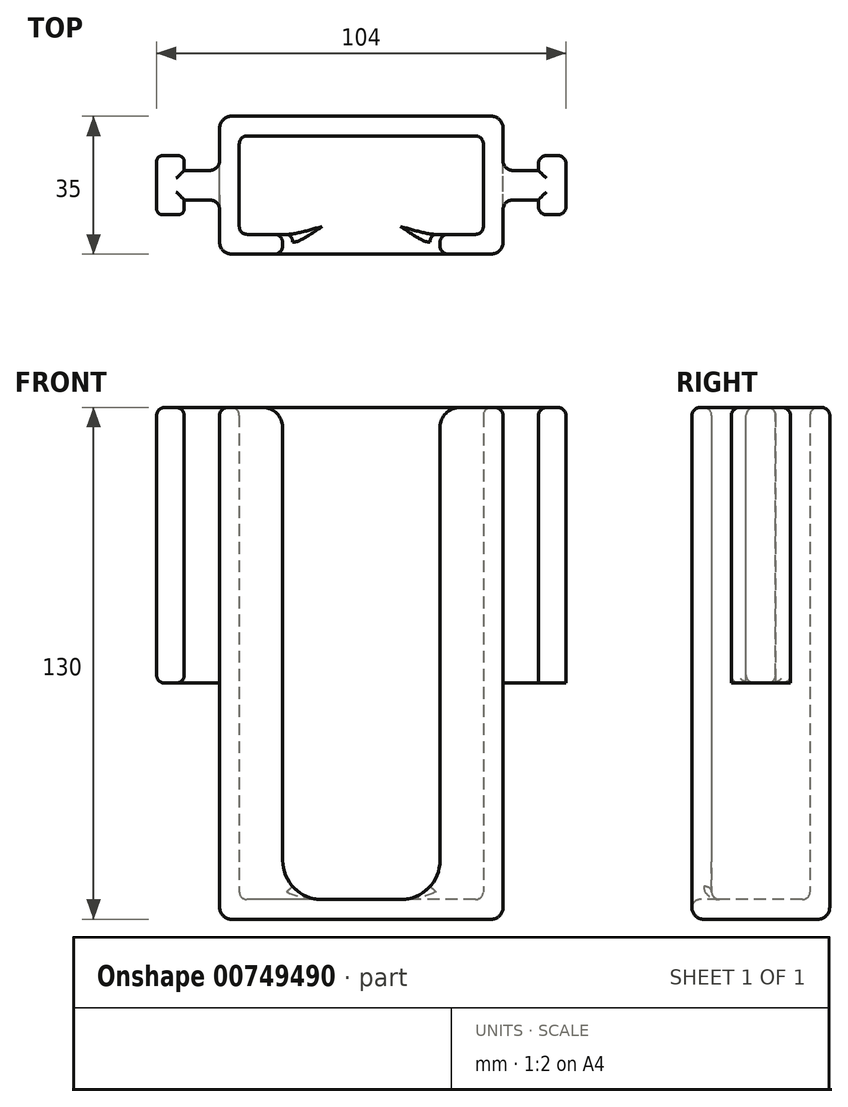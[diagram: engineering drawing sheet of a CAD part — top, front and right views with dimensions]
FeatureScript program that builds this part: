
annotation { "Feature Type Name" : "Feature", "Feature Type Description" : "" }
export const myFeature = defineFeature(function(context is Context, id is Id, definition is map)
    precondition{}
    {
        {
            var Q0;
            Q0=qCreatedBy(makeId("Top.planeOp"),FACE);
            var sketch = newSketch(context, id + "F0", { "sketchPlane" : qUnion([Q0])});
            skLineSegment(sketch, "E0.bottom", {"start": v(-36, -17.5) * mm, "end": v(-20, -17.5) * mm});
            skLineSegment(sketch, "E0.top", {"start": v(-36, 17.5) * mm, "end": v(36, 17.5) * mm});
            skLineSegment(sketch, "E0.left", {"start": v(-36, -17.5) * mm, "end": v(-36, 17.5) * mm});
            skLineSegment(sketch, "E0.right", {"start": v(36, -17.5) * mm, "end": v(36, 17.5) * mm});
            skPoint(sketch, "E0.middle", {"position": v(0, 0) * mm});
            skLineSegment(sketch, "E1.0", {"start": v(-31, 12.5) * mm, "end": v(31, 12.5) * mm});
            skLineSegment(sketch, "E2.0", {"start": v(-31, -12.5) * mm, "end": v(-31, 12.5) * mm});
            skLineSegment(sketch, "E3.0", {"start": v(-31, -12.5) * mm, "end": v(-20, -12.5) * mm});
            skLineSegment(sketch, "E4.0", {"start": v(31, -12.5) * mm, "end": v(31, 12.5) * mm});
            skLineSegment(sketch, "E5", {"start": v(0, 0) * mm, "end": v(0, -28.4) * mm, "construction": true});
            skPoint(sketch, "E5.endSnap0", {"position": v(0, -17.5) * mm});
            skLineSegment(sketch, "E6.left", {"start": v(20, -17.5) * mm, "end": v(20, -12.5) * mm});
            skLineSegment(sketch, "E6.right", {"start": v(-20, -17.5) * mm, "end": v(-20, -12.5) * mm});
            skPoint(sketch, "E6.top.end.orphan", {"position": v(-20, 23.15) * mm});
            skPoint(sketch, "E6.top.start.orphan", {"position": v(20, 23.15) * mm});
            skPoint(sketch, "E7.orphan", {"position": v(20, -23.15) * mm});
            skPoint(sketch, "E8.orphan", {"position": v(-20, -23.15) * mm});
            skLineSegment(sketch, "E9.trimOffspring", {"start": v(20, -17.5) * mm, "end": v(36, -17.5) * mm});
            skLineSegment(sketch, "E10.trimOffspring", {"start": v(20, -12.5) * mm, "end": v(31, -12.5) * mm});
            skSolve(sketch);
        }
        {
            var Q0;
            Q0=qSketchRegion(id+"F0",true);
            extrude(context, id + "F1", {"entities" : qUnion([Q0]), "depth" : 130 * mm, "offsetDistance" : 25 * mm});
        }
        {
            var Q0;
            Q0=makeQuery(id+"F1.opExtrude","CAP_FACE",FACE,{"disambiguationData":[OSD([sQuery(id+"F0.wireOp",EDGE,"E0.bottom"),sQuery(id+"F0.wireOp",EDGE,"E0.top"),sQuery(id+"F0.wireOp",EDGE,"E0.left"),sQuery(id+"F0.wireOp",EDGE,"E0.right"),sQuery(id+"F0.wireOp",EDGE,"E1.0"),sQuery(id+"F0.wireOp",EDGE,"E2.0"),sQuery(id+"F0.wireOp",EDGE,"E3.0"),sQuery(id+"F0.wireOp",EDGE,"E4.0"),sQuery(id+"F0.wireOp",EDGE,"E6.left"),sQuery(id+"F0.wireOp",EDGE,"E6.right"),sQuery(id+"F0.wireOp",EDGE,"E9.trimOffspring"),sQuery(id+"F0.wireOp",EDGE,"E10.trimOffspring"),sQuery(id+"F0.wireOp",EDGE,"IRkvV7g0-v9mD-pYis-f96F-TbbmHekLv8gj"),sQuery(id+"F0.wireOp",EDGE,"QO5cX9hJ-v0gT-aGok-YnyB-QvI0shqeIm5u"),sQuery(id+"F0.wireOp",EDGE,"KRxpQDsH-L7Dp-bXyV-FAdG-3MJ6FIuBowDg"),sQuery(id+"F0.wireOp",EDGE,"sfHnhPzn-JGH8-cdMA-6iEX-DSxyVGc1XTFO"),sQuery(id+"F0.wireOp",EDGE,"91842305-e3c2-40cc-aced-38349b886b1d0.MirrorCS"),sQuery(id+"F0.wireOp",EDGE,"94d3a2cc-75a5-47aa-a43e-d49a1ea905040.MirrorCS"),sQuery(id+"F0.wireOp",EDGE,"641dfdc2-e6f7-4d36-90b3-5f185979efa60.MirrorCS"),sQuery(id+"F0.wireOp",EDGE,"ec8827d9-e664-41d8-a1dc-b07d4c33f75e0.MirrorCS"),sQuery(id+"F0.wireOp",EDGE,"820a947f-c23e-4296-92a9-51708547bf04.trimOffspring")])],"isStart":true});
            var sketch = newSketch(context, id + "F2", { "sketchPlane" : qUnion([Q0])});
            skLineSegment(sketch, "E11.bottom", {"start": v(-36, 17.5) * mm, "end": v(36, 17.5) * mm});
            skLineSegment(sketch, "E11.top", {"start": v(-36, -17.5) * mm, "end": v(36, -17.5) * mm});
            skLineSegment(sketch, "E11.left", {"start": v(-36, 17.5) * mm, "end": v(-36, -17.5) * mm});
            skLineSegment(sketch, "E11.right", {"start": v(36, 17.5) * mm, "end": v(36, -17.5) * mm});
            skSolve(sketch);
        }
        {
            var Q0;
            Q0=qSketchRegion(id+"F2",true);
            extrude(context, id + "F3", {"entities" : qUnion([Q0]), "operationType" : NewBodyOperationType.ADD, "oppositeDirection" : true, "depth" : 5 * mm, "offsetDistance" : 25 * mm});
        }
        {
            var Q0;
            Q0=makeQuery(id+"F3.boolean.opBoolean","INTERSECT",EDGE,{"derivedFrom":[makeQuery(id+"F1.opExtrude","SWEPT_FACE",FACE,{"disambiguationData":[OSD([sQuery(id+"F0.wireOp",EDGE,"E6.right")])]}),makeQuery(id+"F3.opExtrude","CAP_FACE",FACE,{"disambiguationData":[OSD([sQuery(id+"F2.wireOp",EDGE,"E11.bottom"),sQuery(id+"F2.wireOp",EDGE,"E11.top"),sQuery(id+"F2.wireOp",EDGE,"E11.left"),sQuery(id+"F2.wireOp",EDGE,"E11.right")])],"isStart":false})]});
            var Q1;
            Q1=makeQuery(id+"F3.boolean.opBoolean","INTERSECT",EDGE,{"derivedFrom":[makeQuery(id+"F1.opExtrude","SWEPT_FACE",FACE,{"disambiguationData":[OSD([sQuery(id+"F0.wireOp",EDGE,"E6.left")])]}),makeQuery(id+"F3.opExtrude","CAP_FACE",FACE,{"disambiguationData":[OSD([sQuery(id+"F2.wireOp",EDGE,"E11.bottom"),sQuery(id+"F2.wireOp",EDGE,"E11.top"),sQuery(id+"F2.wireOp",EDGE,"E11.left"),sQuery(id+"F2.wireOp",EDGE,"E11.right")])],"isStart":false})]});
            fillet(context, id + "F4", {"entities" : qUnion([Q0, Q1]), "radius" : 10 * mm, "tangentPropagation" : true, "allowEdgeOverflow" : false});
        }
        {
            var Q0;
            Q0=makeQuery(id+"F1.opExtrude","CAP_EDGE",EDGE,{"disambiguationData":[OSD([sQuery(id+"F0.wireOp",EDGE,"E6.left")])],"isStart":false});
            var Q1;
            Q1=makeQuery(id+"F1.opExtrude","CAP_EDGE",EDGE,{"disambiguationData":[OSD([sQuery(id+"F0.wireOp",EDGE,"E6.right")])],"isStart":false});
            fillet(context, id + "F5", {"entities" : qUnion([Q0, Q1]), "radius" : 5 * mm, "tangentPropagation" : true, "allowEdgeOverflow" : false});
        }
        {
            var Q0;
            Q0=makeQuery(id+"F1.opExtrude","CAP_EDGE",EDGE,{"disambiguationData":[OSD([sQuery(id+"F0.wireOp",EDGE,"E0.right")])],"isStart":true});
            var Q1;
            Q1=makeQuery(id+"F1.opExtrude","CAP_EDGE",EDGE,{"disambiguationData":[OSD([sQuery(id+"F0.wireOp",EDGE,"E0.left")])],"isStart":true});
            fillet(context, id + "F6", {"entities" : qUnion([Q0, Q1]), "radius" : 3 * mm, "tangentPropagation" : true, "allowEdgeOverflow" : false});
        }
        {
            var Q0;
            Q0=makeQuery(id+"F3.boolean.opBoolean","INTERSECT",EDGE,{"derivedFrom":[makeQuery(id+"F1.opExtrude","SWEPT_FACE",FACE,{"disambiguationData":[OSD([sQuery(id+"F0.wireOp",EDGE,"E4.0")])]}),makeQuery(id+"F3.opExtrude","CAP_FACE",FACE,{"disambiguationData":[OSD([sQuery(id+"F2.wireOp",EDGE,"E11.bottom"),sQuery(id+"F2.wireOp",EDGE,"E11.top"),sQuery(id+"F2.wireOp",EDGE,"E11.left"),sQuery(id+"F2.wireOp",EDGE,"E11.right")])],"isStart":false})]});
            var Q1;
            Q1=makeQuery(id+"F3.boolean.opBoolean","INTERSECT",EDGE,{"derivedFrom":[makeQuery(id+"F1.opExtrude","SWEPT_FACE",FACE,{"disambiguationData":[OSD([sQuery(id+"F0.wireOp",EDGE,"E1.0")])]}),makeQuery(id+"F3.opExtrude","CAP_FACE",FACE,{"disambiguationData":[OSD([sQuery(id+"F2.wireOp",EDGE,"E11.bottom"),sQuery(id+"F2.wireOp",EDGE,"E11.top"),sQuery(id+"F2.wireOp",EDGE,"E11.left"),sQuery(id+"F2.wireOp",EDGE,"E11.right")])],"isStart":false})]});
            var Q2;
            Q2=makeQuery(id+"F3.boolean.opBoolean","INTERSECT",EDGE,{"derivedFrom":[makeQuery(id+"F1.opExtrude","SWEPT_FACE",FACE,{"disambiguationData":[OSD([sQuery(id+"F0.wireOp",EDGE,"E2.0")])]}),makeQuery(id+"F3.opExtrude","CAP_FACE",FACE,{"disambiguationData":[OSD([sQuery(id+"F2.wireOp",EDGE,"E11.bottom"),sQuery(id+"F2.wireOp",EDGE,"E11.top"),sQuery(id+"F2.wireOp",EDGE,"E11.left"),sQuery(id+"F2.wireOp",EDGE,"E11.right")])],"isStart":false})]});
            fillet(context, id + "F7", {"entities" : qUnion([Q0, Q1, Q2]), "radius" : 2 * mm, "tangentPropagation" : true, "allowEdgeOverflow" : false});
        }
        {
            var Q0;
            Q0=makeQuery(id+"F1.opExtrude","SWEPT_EDGE",EDGE,{"disambiguationData":[OSD([sQuery(id+"F0.wireOp",EDGE,"E1.0"),sQuery(id+"F0.wireOp",EDGE,"E2.0")])]});
            var Q1;
            Q1=makeQuery(id+"F1.opExtrude","SWEPT_EDGE",EDGE,{"disambiguationData":[OSD([sQuery(id+"F0.wireOp",EDGE,"E2.0"),sQuery(id+"F0.wireOp",EDGE,"E3.0")])]});
            var Q2;
            Q2=makeQuery(id+"F1.opExtrude","SWEPT_EDGE",EDGE,{"disambiguationData":[OSD([sQuery(id+"F0.wireOp",EDGE,"E1.0"),sQuery(id+"F0.wireOp",EDGE,"E4.0")])]});
            var Q3;
            Q3=makeQuery(id+"F1.opExtrude","SWEPT_EDGE",EDGE,{"disambiguationData":[OSD([sQuery(id+"F0.wireOp",EDGE,"E4.0"),sQuery(id+"F0.wireOp",EDGE,"E10.trimOffspring")])]});
            fillet(context, id + "F8", {"entities" : qUnion([Q0, Q1, Q2, Q3]), "radius" : 2 * mm, "tangentPropagation" : true, "allowEdgeOverflow" : false});
        }
        {
            var Q0;
            Q0=makeQuery(id+"F1.opExtrude","SWEPT_EDGE",EDGE,{"disambiguationData":[OSD([sQuery(id+"F0.wireOp",EDGE,"E0.right"),sQuery(id+"F0.wireOp",EDGE,"E9.trimOffspring")])]});
            var Q1;
            Q1=makeQuery(id+"F1.opExtrude","SWEPT_EDGE",EDGE,{"disambiguationData":[OSD([sQuery(id+"F0.wireOp",EDGE,"E0.bottom"),sQuery(id+"F0.wireOp",EDGE,"E0.left")])]});
            var Q2;
            Q2=makeQuery(id+"F1.opExtrude","SWEPT_EDGE",EDGE,{"disambiguationData":[OSD([sQuery(id+"F0.wireOp",EDGE,"E0.right"),sQuery(id+"F0.wireOp",EDGE,"820a947f-c23e-4296-92a9-51708547bf04.trimOffspring")])]});
            var Q3;
            Q3=makeQuery(id+"F1.opExtrude","SWEPT_EDGE",EDGE,{"disambiguationData":[OSD([sQuery(id+"F0.wireOp",EDGE,"E0.top"),sQuery(id+"F0.wireOp",EDGE,"E0.left")])]});
            fillet(context, id + "F9", {"entities" : qUnion([Q0, Q1, Q2, Q3]), "radius" : 3 * mm, "tangentPropagation" : true, "allowEdgeOverflow" : false});
        }
        {
            var Q0;
            Q0=makeQuery(id+"F1.opExtrude","CAP_FACE",FACE,{"disambiguationData":[OSD([sQuery(id+"F0.wireOp",EDGE,"E0.bottom"),sQuery(id+"F0.wireOp",EDGE,"E0.top"),sQuery(id+"F0.wireOp",EDGE,"E0.left"),sQuery(id+"F0.wireOp",EDGE,"E0.right"),sQuery(id+"F0.wireOp",EDGE,"E1.0"),sQuery(id+"F0.wireOp",EDGE,"E2.0"),sQuery(id+"F0.wireOp",EDGE,"E3.0"),sQuery(id+"F0.wireOp",EDGE,"E4.0"),sQuery(id+"F0.wireOp",EDGE,"E6.left"),sQuery(id+"F0.wireOp",EDGE,"E6.right"),sQuery(id+"F0.wireOp",EDGE,"E9.trimOffspring"),sQuery(id+"F0.wireOp",EDGE,"E10.trimOffspring"),sQuery(id+"F0.wireOp",EDGE,"IRkvV7g0-v9mD-pYis-f96F-TbbmHekLv8gj"),sQuery(id+"F0.wireOp",EDGE,"QO5cX9hJ-v0gT-aGok-YnyB-QvI0shqeIm5u"),sQuery(id+"F0.wireOp",EDGE,"KRxpQDsH-L7Dp-bXyV-FAdG-3MJ6FIuBowDg"),sQuery(id+"F0.wireOp",EDGE,"sfHnhPzn-JGH8-cdMA-6iEX-DSxyVGc1XTFO"),sQuery(id+"F0.wireOp",EDGE,"91842305-e3c2-40cc-aced-38349b886b1d0.MirrorCS"),sQuery(id+"F0.wireOp",EDGE,"94d3a2cc-75a5-47aa-a43e-d49a1ea905040.MirrorCS"),sQuery(id+"F0.wireOp",EDGE,"641dfdc2-e6f7-4d36-90b3-5f185979efa60.MirrorCS"),sQuery(id+"F0.wireOp",EDGE,"ec8827d9-e664-41d8-a1dc-b07d4c33f75e0.MirrorCS"),sQuery(id+"F0.wireOp",EDGE,"820a947f-c23e-4296-92a9-51708547bf04.trimOffspring")])],"isStart":false});
            var sketch = newSketch(context, id + "F10", { "sketchPlane" : qUnion([Q0])});
            skLineSegment(sketch, "E12", {"start": v(-52, -7.5) * mm, "end": v(-52, 7.5) * mm});
            skLineSegment(sketch, "E13", {"start": v(-52, 7.5) * mm, "end": v(-45, 7.5) * mm});
            skLineSegment(sketch, "E14.MirrorCS", {"start": v(-52, -7.5) * mm, "end": v(-45, -7.5) * mm});
            skPoint(sketch, "E15.orphan", {"position": v(-52, -16.91) * mm});
            skPoint(sketch, "E16.orphan", {"position": v(-52, 31.91) * mm});
            skLineSegment(sketch, "E17", {"start": v(-45, -7.5) * mm, "end": v(-45, -3.75) * mm});
            skLineSegment(sketch, "E18", {"start": v(-45, 3.75) * mm, "end": v(-33.16, 3.75) * mm});
            skLineSegment(sketch, "E19.MirrorCS", {"start": v(-45, -3.75) * mm, "end": v(-33.1, -3.75) * mm});
            skPoint(sketch, "E20.orphan", {"position": v(-40.23, 3.75) * mm});
            skPoint(sketch, "E21.orphan", {"position": v(-40.23, -3.75) * mm});
            skPoint(sketch, "E22.orphan", {"position": v(-52, 3.75) * mm});
            skPoint(sketch, "E23.orphan", {"position": v(-52, -3.75) * mm});
            skLineSegment(sketch, "E24.trimOffspring", {"start": v(-45, 3.75) * mm, "end": v(-45, 7.5) * mm});
            skPoint(sketch, "E25.orphan", {"position": v(-37.24, -7.5) * mm});
            skPoint(sketch, "E26.orphan", {"position": v(-37.24, 7.5) * mm});
            skLineSegment(sketch, "E27", {"start": v(-33.1, -3.75) * mm, "end": v(-33.16, 3.75) * mm});
            skLineSegment(sketch, "E28", {"start": v(0, 17.5) * mm, "end": v(0, -29.53) * mm, "construction": true});
            skLineSegment(sketch, "E29.MirrorCS", {"start": v(52, 7.5) * mm, "end": v(45, 7.5) * mm});
            skLineSegment(sketch, "E30.MirrorCS", {"start": v(52, -7.5) * mm, "end": v(52, 7.5) * mm});
            skLineSegment(sketch, "E31.MirrorCS", {"start": v(52, -7.5) * mm, "end": v(45, -7.5) * mm});
            skLineSegment(sketch, "E32.MirrorCS", {"start": v(45, -7.5) * mm, "end": v(45, -3.75) * mm});
            skLineSegment(sketch, "E33.MirrorCS", {"start": v(45, 3.75) * mm, "end": v(45, 7.5) * mm});
            skLineSegment(sketch, "E34.MirrorCS", {"start": v(45, 3.75) * mm, "end": v(33.16, 3.75) * mm});
            skLineSegment(sketch, "E35.MirrorCS", {"start": v(45, -3.75) * mm, "end": v(33.1, -3.75) * mm});
            skLineSegment(sketch, "E36.MirrorCS", {"start": v(33.1, -3.75) * mm, "end": v(33.16, 3.75) * mm});
            skSolve(sketch);
        }
        {
            var Q0;
            Q0=makeQuery(id+"F10.imprint","IMPRINT",FACE,{"disambiguationData":[TD([[makeQuery(id+"F10.imprint","IMPRINT",EDGE,{"derivedFrom":sQuery(id+"F10.wireOp",EDGE,"E12")}),-1.0]])]});
            var Q1;
            {var subQ0=sQuery(id+"F10.wireOp",EDGE,"E27");Q1=makeQuery(id+"F10.imprint","IMPRINT",FACE,{"disambiguationData":[TD([[makeQuery(id+"F10.imprint","IMPRINT",EDGE,{"derivedFrom":subQ0}),1.0]])]});}
            var Q2;
            {var subQ0=sQuery(id+"F10.wireOp",EDGE,"E36.MirrorCS");Q2=makeQuery(id+"F10.imprint","IMPRINT",FACE,{"disambiguationData":[TD([[makeQuery(id+"F10.imprint","IMPRINT",EDGE,{"derivedFrom":subQ0}),-1.0]])]});}
            var Q3;
            Q3=makeQuery(id+"F10.imprint","IMPRINT",FACE,{"disambiguationData":[TD([[makeQuery(id+"F10.imprint","IMPRINT",EDGE,{"derivedFrom":sQuery(id+"F10.wireOp",EDGE,"E29.MirrorCS")}),1.0]])]});
            extrude(context, id + "F11", {"entities" : qUnion([Q0, Q1, Q2, Q3]), "operationType" : NewBodyOperationType.ADD, "oppositeDirection" : true, "depth" : 70 * mm, "offsetDistance" : 25 * mm});
        }
        {
            var Q0;
            Q0=makeQuery(id+"F11.opExtrude","SWEPT_EDGE",EDGE,{"disambiguationData":[OSD([sQuery(id+"F10.wireOp",EDGE,"E12"),sQuery(id+"F10.wireOp",EDGE,"E13")])]});
            var Q1;
            Q1=makeQuery(id+"F11.opExtrude","SWEPT_EDGE",EDGE,{"disambiguationData":[OSD([sQuery(id+"F10.wireOp",EDGE,"E12"),sQuery(id+"F10.wireOp",EDGE,"E14.MirrorCS")])]});
            var Q2;
            Q2=makeQuery(id+"F11.opExtrude","SWEPT_EDGE",EDGE,{"disambiguationData":[OSD([sQuery(id+"F10.wireOp",EDGE,"E14.MirrorCS"),sQuery(id+"F10.wireOp",EDGE,"E17")])]});
            var Q3;
            Q3=makeQuery(id+"F11.opExtrude","SWEPT_EDGE",EDGE,{"disambiguationData":[OSD([sQuery(id+"F10.wireOp",EDGE,"E13"),sQuery(id+"F10.wireOp",EDGE,"E24.trimOffspring")])]});
            fillet(context, id + "F12", {"entities" : qUnion([Q0, Q1, Q2, Q3]), "radius" : 1.5 * mm, "tangentPropagation" : true, "allowEdgeOverflow" : false});
        }
        {
            var Q0;
            Q0=makeQuery(id+"F11.boolean.opBoolean","INTERSECT",EDGE,{"derivedFrom":[makeQuery(id+"F1.opExtrude","SWEPT_FACE",FACE,{"disambiguationData":[OSD([sQuery(id+"F0.wireOp",EDGE,"E0.left")])]}),makeQuery(id+"F11.opExtrude","SWEPT_FACE",FACE,{"disambiguationData":[OSD([sQuery(id+"F10.wireOp",EDGE,"E18")])]})]});
            var Q1;
            Q1=makeQuery(id+"F11.boolean.opBoolean","INTERSECT",EDGE,{"derivedFrom":[makeQuery(id+"F1.opExtrude","SWEPT_FACE",FACE,{"disambiguationData":[OSD([sQuery(id+"F0.wireOp",EDGE,"E0.left")])]}),makeQuery(id+"F11.opExtrude","SWEPT_FACE",FACE,{"disambiguationData":[OSD([sQuery(id+"F10.wireOp",EDGE,"E19.MirrorCS")])]})]});
            fillet(context, id + "F13", {"entities" : qUnion([Q0, Q1]), "radius" : 2.5 * mm, "tangentPropagation" : true, "allowEdgeOverflow" : false});
        }
        {
            var Q0;
            Q0=makeQuery(id+"F11.opExtrude","CAP_EDGE",EDGE,{"disambiguationData":[OSD([sQuery(id+"F10.wireOp",EDGE,"E12")])],"isStart":true});
            fillet(context, id + "F14", {"entities" : qUnion([Q0]), "radius" : 2 * mm, "tangentPropagation" : true, "allowEdgeOverflow" : false});
        }
        {
            var Q0;
            Q0=makeQuery(id+"F1.opExtrude","CAP_EDGE",EDGE,{"disambiguationData":[OSD([sQuery(id+"F0.wireOp",EDGE,"E2.0")])],"isStart":false});
            var Q1;
            Q1=makeQuery(id+"F1.opExtrude","CAP_EDGE",EDGE,{"disambiguationData":[OSD([sQuery(id+"F0.wireOp",EDGE,"E4.0")])],"isStart":false});
            fillet(context, id + "F15", {"entities" : qUnion([Q0, Q1]), "radius" : 2 * mm, "tangentPropagation" : true, "allowEdgeOverflow" : false});
        }
        {
            var Q0;
            Q0=makeQuery(id+"F11.opExtrude","CAP_EDGE",EDGE,{"disambiguationData":[OSD([sQuery(id+"F10.wireOp",EDGE,"E12")])],"isStart":false});
            var Q1;
            Q1=makeQuery(id+"F11.opExtrude","CAP_EDGE",EDGE,{"disambiguationData":[OSD([sQuery(id+"F10.wireOp",EDGE,"E18")])],"isStart":false});
            fillet(context, id + "F16", {"entities" : qUnion([Q0, Q1]), "radius" : 2 * mm, "tangentPropagation" : true, "allowEdgeOverflow" : false});
        }
        {
            var Q0;
            Q0=makeQuery(id+"F11.opExtrude","CAP_EDGE",EDGE,{"disambiguationData":[OSD([sQuery(id+"F10.wireOp",EDGE,"E19.MirrorCS")])],"isStart":false});
            fillet(context, id + "F17", {"entities" : qUnion([Q0]), "radius" : 2 * mm, "tangentPropagation" : true, "allowEdgeOverflow" : false});
        }
        {
            var Q0;
            Q0=makeQuery(id+"F11.opExtrude","CAP_EDGE",EDGE,{"disambiguationData":[OSD([sQuery(id+"F10.wireOp",EDGE,"E19.MirrorCS")])],"isStart":true});
            var Q1;
            {var subQ0=sQuery(id+"F0.wireOp",EDGE,"E0.left");var subQ2=sQuery(id+"F10.wireOp",EDGE,"E19.MirrorCS");Q1=makeQuery(id+"F11.boolean.opBoolean","SPLIT",EDGE,{"disambiguationData":[TD([makeQuery(id+"F11.opExtrude","SWEPT_FACE",FACE,{"disambiguationData":[OSD([subQ2])]})])],"derivedFrom":makeQuery(id+"F1.opExtrude","CAP_EDGE",EDGE,{"disambiguationData":[OSD([subQ0])],"isStart":false})});}
            var Q2;
            Q2=makeQuery(id+"F1.opExtrude","CAP_EDGE",EDGE,{"disambiguationData":[OSD([sQuery(id+"F0.wireOp",EDGE,"E0.bottom")])],"isStart":false});
            var Q3;
            Q3=makeQuery(id+"F11.opExtrude","CAP_EDGE",EDGE,{"disambiguationData":[OSD([sQuery(id+"F10.wireOp",EDGE,"E18")])],"isStart":true});
            var Q4;
            {var subQ0=sQuery(id+"F10.wireOp",EDGE,"E18");var subQ1=sQuery(id+"F0.wireOp",EDGE,"E0.left");Q4=makeQuery(id+"F11.boolean.opBoolean","SPLIT",EDGE,{"disambiguationData":[TD([makeQuery(id+"F11.opExtrude","SWEPT_FACE",FACE,{"disambiguationData":[OSD([subQ0])]})])],"derivedFrom":makeQuery(id+"F1.opExtrude","CAP_EDGE",EDGE,{"disambiguationData":[OSD([subQ1])],"isStart":false})});}
            fillet(context, id + "F18", {"entities" : qUnion([Q0, Q1, Q2, Q3, Q4]), "radius" : 2 * mm, "tangentPropagation" : true, "allowEdgeOverflow" : false});
        }
        {
            var Q0;
            Q0=makeQuery(id+"F11.boolean.opBoolean","INTERSECT",EDGE,{"derivedFrom":[makeQuery(id+"F1.opExtrude","SWEPT_FACE",FACE,{"disambiguationData":[OSD([sQuery(id+"F0.wireOp",EDGE,"E0.right")])]}),makeQuery(id+"F11.opExtrude","SWEPT_FACE",FACE,{"disambiguationData":[OSD([sQuery(id+"F10.wireOp",EDGE,"E35.MirrorCS")])]})]});
            var Q1;
            Q1=makeQuery(id+"F11.boolean.opBoolean","INTERSECT",EDGE,{"derivedFrom":[makeQuery(id+"F1.opExtrude","SWEPT_FACE",FACE,{"disambiguationData":[OSD([sQuery(id+"F0.wireOp",EDGE,"E0.right")])]}),makeQuery(id+"F11.opExtrude","SWEPT_FACE",FACE,{"disambiguationData":[OSD([sQuery(id+"F10.wireOp",EDGE,"E34.MirrorCS")])]})]});
            fillet(context, id + "F19", {"entities" : qUnion([Q0, Q1]), "radius" : 2.5 * mm, "tangentPropagation" : true, "allowEdgeOverflow" : false});
        }
        {
            var Q0;
            Q0=makeQuery(id+"F11.opExtrude","CAP_EDGE",EDGE,{"disambiguationData":[OSD([sQuery(id+"F10.wireOp",EDGE,"E35.MirrorCS")])],"isStart":true});
            var Q1;
            Q1=makeQuery(id+"F11.opExtrude","CAP_EDGE",EDGE,{"disambiguationData":[OSD([sQuery(id+"F10.wireOp",EDGE,"E32.MirrorCS")])],"isStart":true});
            var Q2;
            Q2=makeQuery(id+"F11.opExtrude","CAP_EDGE",EDGE,{"disambiguationData":[OSD([sQuery(id+"F10.wireOp",EDGE,"E31.MirrorCS")])],"isStart":true});
            var Q3;
            Q3=makeQuery(id+"F11.opExtrude","CAP_EDGE",EDGE,{"disambiguationData":[OSD([sQuery(id+"F10.wireOp",EDGE,"E30.MirrorCS")])],"isStart":true});
            var Q4;
            Q4=makeQuery(id+"F11.opExtrude","CAP_EDGE",EDGE,{"disambiguationData":[OSD([sQuery(id+"F10.wireOp",EDGE,"E29.MirrorCS")])],"isStart":true});
            var Q5;
            Q5=makeQuery(id+"F11.opExtrude","CAP_EDGE",EDGE,{"disambiguationData":[OSD([sQuery(id+"F10.wireOp",EDGE,"E33.MirrorCS")])],"isStart":true});
            var Q6;
            Q6=makeQuery(id+"F11.opExtrude","CAP_EDGE",EDGE,{"disambiguationData":[OSD([sQuery(id+"F10.wireOp",EDGE,"E34.MirrorCS")])],"isStart":true});
            fillet(context, id + "F20", {"entities" : qUnion([Q0, Q1, Q2, Q3, Q4, Q5, Q6]), "radius" : 2 * mm, "tangentPropagation" : true, "allowEdgeOverflow" : false});
        }
        {
            var Q0;
            Q0=makeQuery(id+"F11.opExtrude","SWEPT_EDGE",EDGE,{"disambiguationData":[OSD([sQuery(id+"F10.wireOp",EDGE,"E29.MirrorCS"),sQuery(id+"F10.wireOp",EDGE,"E30.MirrorCS")])]});
            var Q1;
            Q1=makeQuery(id+"F11.opExtrude","SWEPT_EDGE",EDGE,{"disambiguationData":[OSD([sQuery(id+"F10.wireOp",EDGE,"E30.MirrorCS"),sQuery(id+"F10.wireOp",EDGE,"E31.MirrorCS")])]});
            fillet(context, id + "F21", {"entities" : qUnion([Q0, Q1]), "radius" : 2 * mm, "tangentPropagation" : true, "allowEdgeOverflow" : false});
        }
        {
            var Q0;
            Q0=makeQuery(id+"F11.opExtrude","SWEPT_EDGE",EDGE,{"disambiguationData":[OSD([sQuery(id+"F10.wireOp",EDGE,"E31.MirrorCS"),sQuery(id+"F10.wireOp",EDGE,"E32.MirrorCS")])]});
            var Q1;
            Q1=makeQuery(id+"F11.opExtrude","SWEPT_EDGE",EDGE,{"disambiguationData":[OSD([sQuery(id+"F10.wireOp",EDGE,"E29.MirrorCS"),sQuery(id+"F10.wireOp",EDGE,"E33.MirrorCS")])]});
            fillet(context, id + "F22", {"entities" : qUnion([Q0, Q1]), "radius" : 2 * mm, "tangentPropagation" : true, "allowEdgeOverflow" : false});
        }
    });
